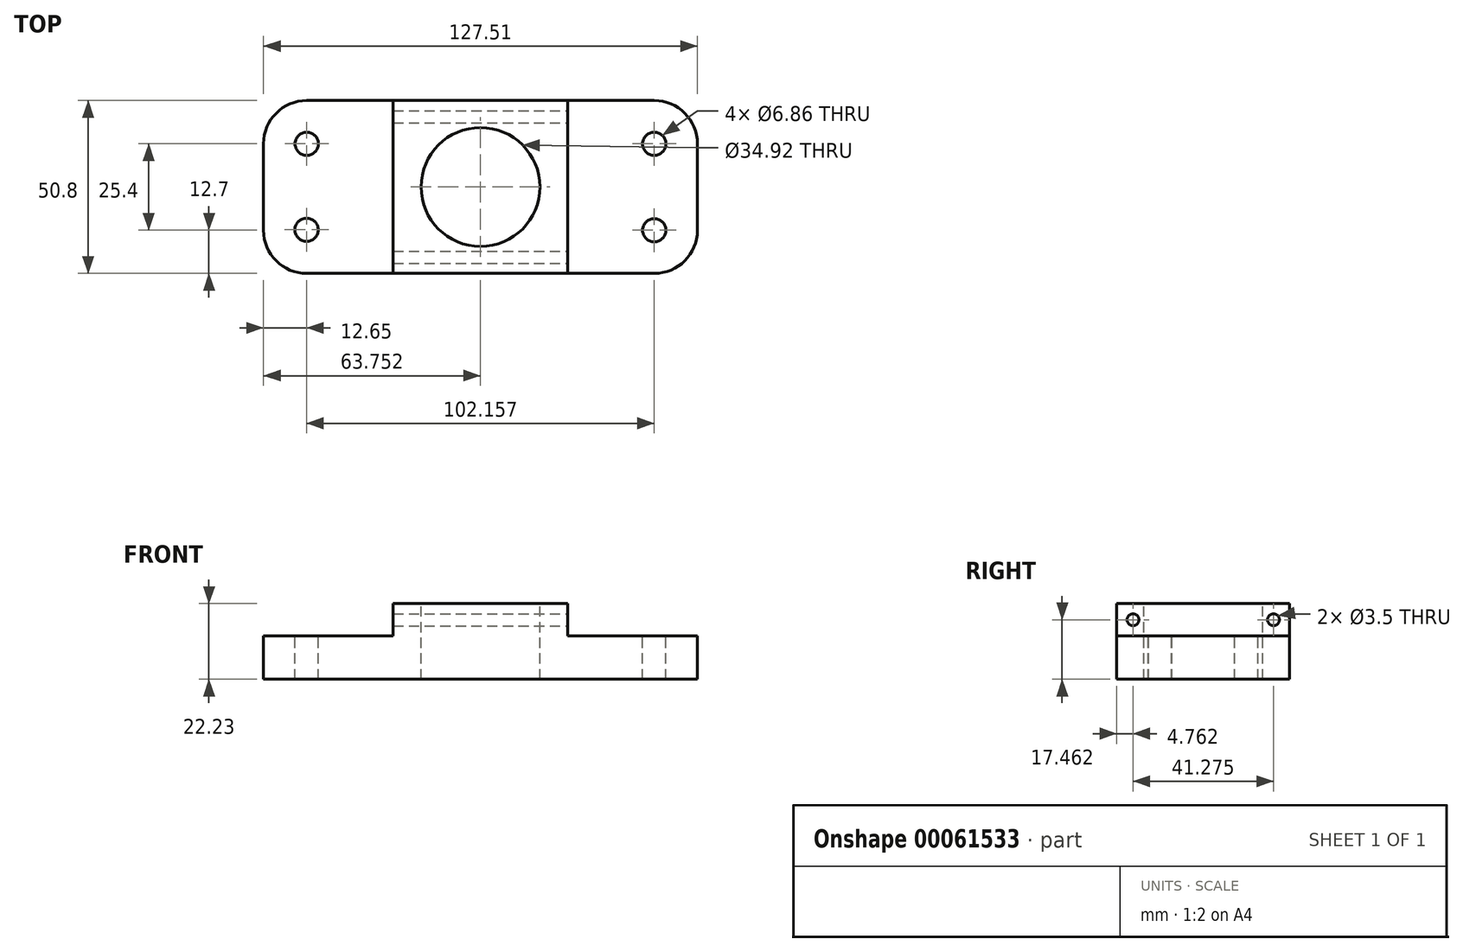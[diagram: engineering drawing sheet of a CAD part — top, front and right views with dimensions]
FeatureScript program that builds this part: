
annotation { "Feature Type Name" : "Feature", "Feature Type Description" : "" }
export const myFeature = defineFeature(function(context is Context, id is Id, definition is map)
    precondition{}
    {
        {
            var Q0;
            Q0=qCreatedBy(makeId("Front.planeOp"),FACE);
            var sketch = newSketch(context, id + "F0", { "sketchPlane" : qUnion([Q0])});
            skLineSegment(sketch, "E0.bottom", {"start": v(-16.85, 22.22) * mm, "end": v(34.46, 22.22) * mm});
            skLineSegment(sketch, "E0.top", {"start": v(-54.95, 0) * mm, "end": v(72.56, 0) * mm});
            skLineSegment(sketch, "E0.left", {"start": v(-54.95, 12.7) * mm, "end": v(-54.95, 0) * mm});
            skLineSegment(sketch, "E0.right", {"start": v(72.56, 12.7) * mm, "end": v(72.56, 0) * mm});
            skLineSegment(sketch, "E1.top", {"start": v(-54.95, 12.7) * mm, "end": v(-16.85, 12.7) * mm});
            skLineSegment(sketch, "E1.right", {"start": v(-16.85, 22.22) * mm, "end": v(-16.85, 12.7) * mm});
            skLineSegment(sketch, "E2.top", {"start": v(34.46, 12.7) * mm, "end": v(72.56, 12.7) * mm});
            skLineSegment(sketch, "E2.left", {"start": v(34.46, 22.22) * mm, "end": v(34.46, 12.7) * mm});
            skSolve(sketch);
        }
        {
            var Q0;
            Q0 = qSketchRegion(id + "F0", true);
            extrude(context, id + "F1", {"entities" : qUnion([Q0]), "depth" : 50.8 * mm});
        }
        {
            var Q0;
            Q0=makeQuery(id+"F1.opExtrude","CAP_EDGE",EDGE,{"disambiguationData":[OSD([sQuery(id+"F0.wireOp",EDGE,"E0.right")])],"isStart":false});
            var Q1;
            Q1=makeQuery(id+"F1.opExtrude","CAP_EDGE",EDGE,{"disambiguationData":[OSD([sQuery(id+"F0.wireOp",EDGE,"E0.right")])],"isStart":true});
            var Q2;
            Q2=makeQuery(id+"F1.opExtrude","CAP_EDGE",EDGE,{"disambiguationData":[OSD([sQuery(id+"F0.wireOp",EDGE,"E0.left")])],"isStart":false});
            var Q3;
            Q3=makeQuery(id+"F1.opExtrude","CAP_EDGE",EDGE,{"disambiguationData":[OSD([sQuery(id+"F0.wireOp",EDGE,"E0.left")])],"isStart":true});
            fillet(context, id + "F2", {"entities" : qUnion([Q0, Q1, Q2, Q3]), "radius" : 12.7 * mm, "tangentPropagation" : true, "allowEdgeOverflow" : false});
        }
        {
            var Q0;
            Q0=makeQuery(id+"F1.opExtrude","SWEPT_FACE",FACE,{"disambiguationData":[OSD([sQuery(id+"F0.wireOp",EDGE,"E1.top")])]});
            var sketch = newSketch(context, id + "F3", { "sketchPlane" : qUnion([Q0])});
            skCircle(sketch, "E3", {"center": v(-42.25, -12.7) * mm, "radius": 3.43 * mm});
            skPoint(sketch, "E4", {"position": v(-42.25, -38.1) * mm});
            skPoint(sketch, "E5", {"position": v(59.86, -38.1) * mm});
            skPoint(sketch, "E6", {"position": v(59.86, -12.7) * mm});
            skPoint(sketch, "E7.0", {"position": v(-16.85, 0) * mm});
            skPoint(sketch, "E8.0", {"position": v(34.46, -50.8) * mm});
            skPoint(sketch, "E9.0", {"position": v(34.46, 0) * mm});
            skPoint(sketch, "E10.0", {"position": v(-16.85, -50.8) * mm});
            skLineSegment(sketch, "E11", {"start": v(-16.85, 0) * mm, "end": v(34.46, -50.8) * mm, "construction": true});
            skLineSegment(sketch, "E12", {"start": v(34.46, 0) * mm, "end": v(-16.85, -50.8) * mm, "construction": true});
            skCircle(sketch, "E13", {"center": v(8.8, -25.4) * mm, "radius": 17.46 * mm});
            skCircle(sketch, "E14", {"center": v(59.86, -38.1) * mm, "radius": 3.43 * mm});
            skCircle(sketch, "E15", {"center": v(-42.3, -37.97) * mm, "radius": 3.43 * mm});
            skCircle(sketch, "E16", {"center": v(59.86, -12.7) * mm, "radius": 3.43 * mm});
            skSolve(sketch);
        }
        {
            var Q0;
            Q0 = qSketchRegion(id + "F3", true);
            extrude(context, id + "F4", {"entities" : qUnion([Q0]), "operationType" : NewBodyOperationType.REMOVE, "oppositeDirection" : true, "depth" : 25.4 * mm, "hasSecondDirection" : true, "secondDirectionOppositeDirection" : false, "secondDirectionDepth" : 25.4 * mm});
        }
        {
            var Q0;
            Q0=makeQuery(id+"F1.opExtrude","SWEPT_FACE",FACE,{"disambiguationData":[OSD([sQuery(id+"F0.wireOp",EDGE,"E2.left")])]});
            var sketch = newSketch(context, id + "F5", { "sketchPlane" : qUnion([Q0])});
            skCircle(sketch, "E17", {"center": v(-46.04, 17.46) * mm, "radius": 1.75 * mm});
            skCircle(sketch, "E18", {"center": v(-4.76, 17.46) * mm, "radius": 1.75 * mm});
            skSolve(sketch);
        }
        {
            var Q0;
            Q0 = qSketchRegion(id + "F5", true);
            extrude(context, id + "F6", {"entities" : qUnion([Q0]), "operationType" : NewBodyOperationType.REMOVE, "endBound" : BoundingType.THROUGH_ALL, "oppositeDirection" : true, "depth" : 25.4 * mm});
        }
    });
